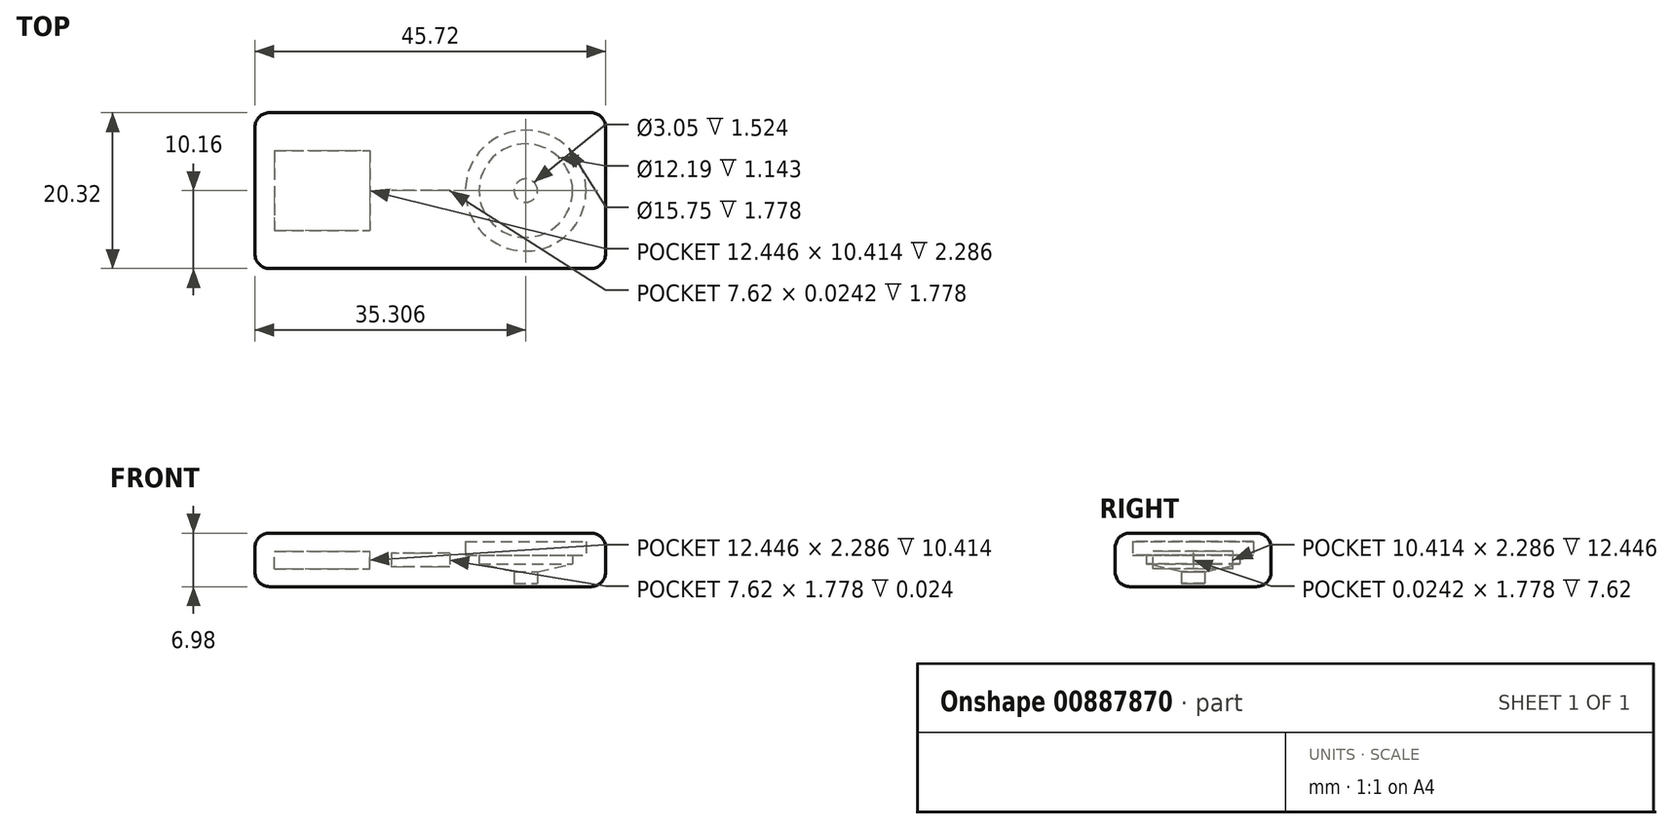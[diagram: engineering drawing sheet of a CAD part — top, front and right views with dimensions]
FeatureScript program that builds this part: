
annotation { "Feature Type Name" : "Feature", "Feature Type Description" : "" }
export const myFeature = defineFeature(function(context is Context, id is Id, definition is map)
    precondition{}
    {
        {
            var Q0;
            Q0=qCreatedBy(makeId("Front.planeOp"),FACE);
            var sketch = newSketch(context, id + "F0", { "sketchPlane" : qUnion([Q0])});
            skLineSegment(sketch, "E0.bottom", {"start": v(22.86, 3.5) * mm, "end": v(-22.86, 3.5) * mm});
            skLineSegment(sketch, "E0.top", {"start": v(22.86, -3.5) * mm, "end": v(-22.86, -3.5) * mm});
            skLineSegment(sketch, "E0.left", {"start": v(22.86, 3.5) * mm, "end": v(22.86, -3.5) * mm});
            skLineSegment(sketch, "E0.right", {"start": v(-22.86, 3.5) * mm, "end": v(-22.86, -3.5) * mm});
            skPoint(sketch, "E0.middle", {"position": v(0, 0) * mm});
            skSolve(sketch);
        }
        {
            var Q0;
            Q0 = qSketchRegion(id + "F0", true);
            extrude(context, id + "F1", {"entities" : qUnion([Q0]), "oppositeDirection" : true, "depth" : 10.16 * mm, "offsetDistance" : 25.4 * mm});
        }
        {
            var Q0;
            Q0=makeQuery(id+"F1.opExtrude","CAP_EDGE",EDGE,{"disambiguationData":[OSD([sQuery(id+"F0.wireOp",EDGE,"E0.bottom")])],"isStart":false});
            var Q1;
            Q1=makeQuery(id+"F1.opExtrude","SWEPT_EDGE",EDGE,{"disambiguationData":[OSD([sQuery(id+"F0.wireOp",EDGE,"E0.bottom"),sQuery(id+"F0.wireOp",EDGE,"E0.left")])]});
            var Q2;
            Q2=makeQuery(id+"F1.opExtrude","CAP_EDGE",EDGE,{"disambiguationData":[OSD([sQuery(id+"F0.wireOp",EDGE,"E0.left")])],"isStart":false});
            var Q3;
            Q3=makeQuery(id+"F1.opExtrude","SWEPT_EDGE",EDGE,{"disambiguationData":[OSD([sQuery(id+"F0.wireOp",EDGE,"E0.top"),sQuery(id+"F0.wireOp",EDGE,"E0.left")])]});
            var Q4;
            Q4=makeQuery(id+"F1.opExtrude","CAP_EDGE",EDGE,{"disambiguationData":[OSD([sQuery(id+"F0.wireOp",EDGE,"E0.right")])],"isStart":false});
            var Q5;
            Q5=makeQuery(id+"F1.opExtrude","SWEPT_EDGE",EDGE,{"disambiguationData":[OSD([sQuery(id+"F0.wireOp",EDGE,"E0.top"),sQuery(id+"F0.wireOp",EDGE,"E0.right")])]});
            var Q6;
            Q6=makeQuery(id+"F1.opExtrude","SWEPT_EDGE",EDGE,{"disambiguationData":[OSD([sQuery(id+"F0.wireOp",EDGE,"E0.bottom"),sQuery(id+"F0.wireOp",EDGE,"E0.right")])]});
            var Q7;
            Q7=makeQuery(id+"F1.opExtrude","CAP_EDGE",EDGE,{"disambiguationData":[OSD([sQuery(id+"F0.wireOp",EDGE,"E0.top")])],"isStart":false});
            fillet(context, id + "F2", {"entities" : qUnion([Q0, Q1, Q2, Q3, Q4, Q5, Q6, Q7]), "radius" : 1.9 * mm, "tangentPropagation" : true, "allowEdgeOverflow" : false});
        }
        {
            var Q0;
            Q0=makeQuery(id+"F1.opExtrude","CAP_FACE",FACE,{"disambiguationData":[OSD([sQuery(id+"F0.wireOp",EDGE,"E0.bottom"),sQuery(id+"F0.wireOp",EDGE,"E0.top"),sQuery(id+"F0.wireOp",EDGE,"E0.left"),sQuery(id+"F0.wireOp",EDGE,"E0.right")])],"isStart":true});
            var sketch = newSketch(context, id + "F3", { "sketchPlane" : qUnion([Q0])});
            skLineSegment(sketch, "E1.bottom", {"start": v(-20.32, -1.14) * mm, "end": v(-7.87, -1.14) * mm});
            skLineSegment(sketch, "E1.top", {"start": v(-20.32, 1.14) * mm, "end": v(-7.87, 1.14) * mm});
            skLineSegment(sketch, "E1.left", {"start": v(-20.32, -1.14) * mm, "end": v(-20.32, 1.14) * mm});
            skLineSegment(sketch, "E1.right", {"start": v(-7.87, -1.14) * mm, "end": v(-7.87, 1.14) * mm});
            skSolve(sketch);
        }
        {
            var Q0;
            Q0=makeQuery(id+"F3.imprint","IMPRINT",FACE,{"disambiguationData":[TD([[makeQuery(id+"F3.imprint","IMPRINT",EDGE,{"derivedFrom":sQuery(id+"F3.wireOp",EDGE,"E1.bottom")}),-1.0]])]});
            var sketch = newSketch(context, id + "F4", { "sketchPlane" : qUnion([Q0])});
            skLineSegment(sketch, "E2.bottom", {"start": v(2.54, 0.89) * mm, "end": v(-5.08, 0.89) * mm});
            skLineSegment(sketch, "E2.top", {"start": v(2.54, -0.89) * mm, "end": v(-5.08, -0.89) * mm});
            skLineSegment(sketch, "E2.left", {"start": v(2.54, 0.89) * mm, "end": v(2.54, -0.89) * mm});
            skLineSegment(sketch, "E2.right", {"start": v(-5.08, 0.89) * mm, "end": v(-5.08, -0.89) * mm});
            skSolve(sketch);
        }
        {
            var Q0;
            Q0=makeQuery(id+"F3.imprint","IMPRINT",FACE,{"disambiguationData":[TD([[makeQuery(id+"F3.imprint","IMPRINT",EDGE,{"derivedFrom":sQuery(id+"F3.wireOp",EDGE,"E1.bottom")}),-1.0]])]});
            var sketch = newSketch(context, id + "F5", { "sketchPlane" : qUnion([Q0])});
            skLineSegment(sketch, "E3", {"start": v(18.54, -0.55) * mm, "end": v(13.97, -1.56) * mm});
            skLineSegment(sketch, "E4", {"start": v(13.97, -1.56) * mm, "end": v(13.97, -3.09) * mm});
            skLineSegment(sketch, "E5", {"start": v(13.97, -3.09) * mm, "end": v(12.45, -3.09) * mm});
            skLineSegment(sketch, "E6", {"start": v(18.54, -0.55) * mm, "end": v(18.54, 0.6) * mm});
            skLineSegment(sketch, "E7", {"start": v(18.54, 0.6) * mm, "end": v(20.32, 0.6) * mm});
            skLineSegment(sketch, "E8", {"start": v(20.32, 0.6) * mm, "end": v(20.32, 2.37) * mm});
            skLineSegment(sketch, "E9", {"start": v(20.32, 2.37) * mm, "end": v(12.45, 2.37) * mm});
            skLineSegment(sketch, "E10", {"start": v(12.45, 2.37) * mm, "end": v(12.45, -3.09) * mm});
            skSolve(sketch);
        }
        {
            var Q0;
            Q0 = qSketchRegion(id + "F5", true);
            var Q1;
            Q1=sQuery(id+"F5.wireOp",EDGE,"E10");
            revolve(context, id + "F6", {"operationType" : NewBodyOperationType.REMOVE, "surfaceOperationType" : NewSurfaceOperationType.NEW, "entities" : qUnion([Q0]), "axis" : qUnion([Q1]), "revolveType" : RevolveType.ONE_DIRECTION, "oppositeDirection" : true, "angle" : 180 * degree});
        }
        {
            var Q0;
            Q0 = qSketchRegion(id + "F3", true);
            extrude(context, id + "F7", {"entities" : qUnion([Q0]), "operationType" : NewBodyOperationType.REMOVE, "oppositeDirection" : true, "depth" : 5.2 * mm, "offsetDistance" : 25.4 * mm});
        }
        {
            var Q0;
            Q0 = qSketchRegion(id + "F4", true);
            extrude(context, id + "F8", {"entities" : qUnion([Q0]), "operationType" : NewBodyOperationType.REMOVE, "oppositeDirection" : true, "depth" : .615 / 50.8 * mm, "offsetDistance" : 25.4 * mm});
        }
        {
            var Q0;
            Q0=makeQuery(id+"F1.opExtrude","SWEPT_BODY",BODY,{"disambiguationData":[OSD([sQuery(id+"F0.wireOp",EDGE,"E0.bottom"),sQuery(id+"F0.wireOp",EDGE,"E0.top"),sQuery(id+"F0.wireOp",EDGE,"E0.left"),sQuery(id+"F0.wireOp",EDGE,"E0.right")])]});
            var Q1;
            Q1=makeQuery(id+"F1.opExtrude","CAP_FACE",FACE,{"disambiguationData":[OSD([sQuery(id+"F0.wireOp",EDGE,"E0.bottom"),sQuery(id+"F0.wireOp",EDGE,"E0.top"),sQuery(id+"F0.wireOp",EDGE,"E0.left"),sQuery(id+"F0.wireOp",EDGE,"E0.right")])],"isStart":true});
            mirror(context, id + "F9", {"operationType" : NewBodyOperationType.ADD, "entities" : qUnion([Q0]), "mirrorPlane" : qUnion([Q1])});
        }
    });
